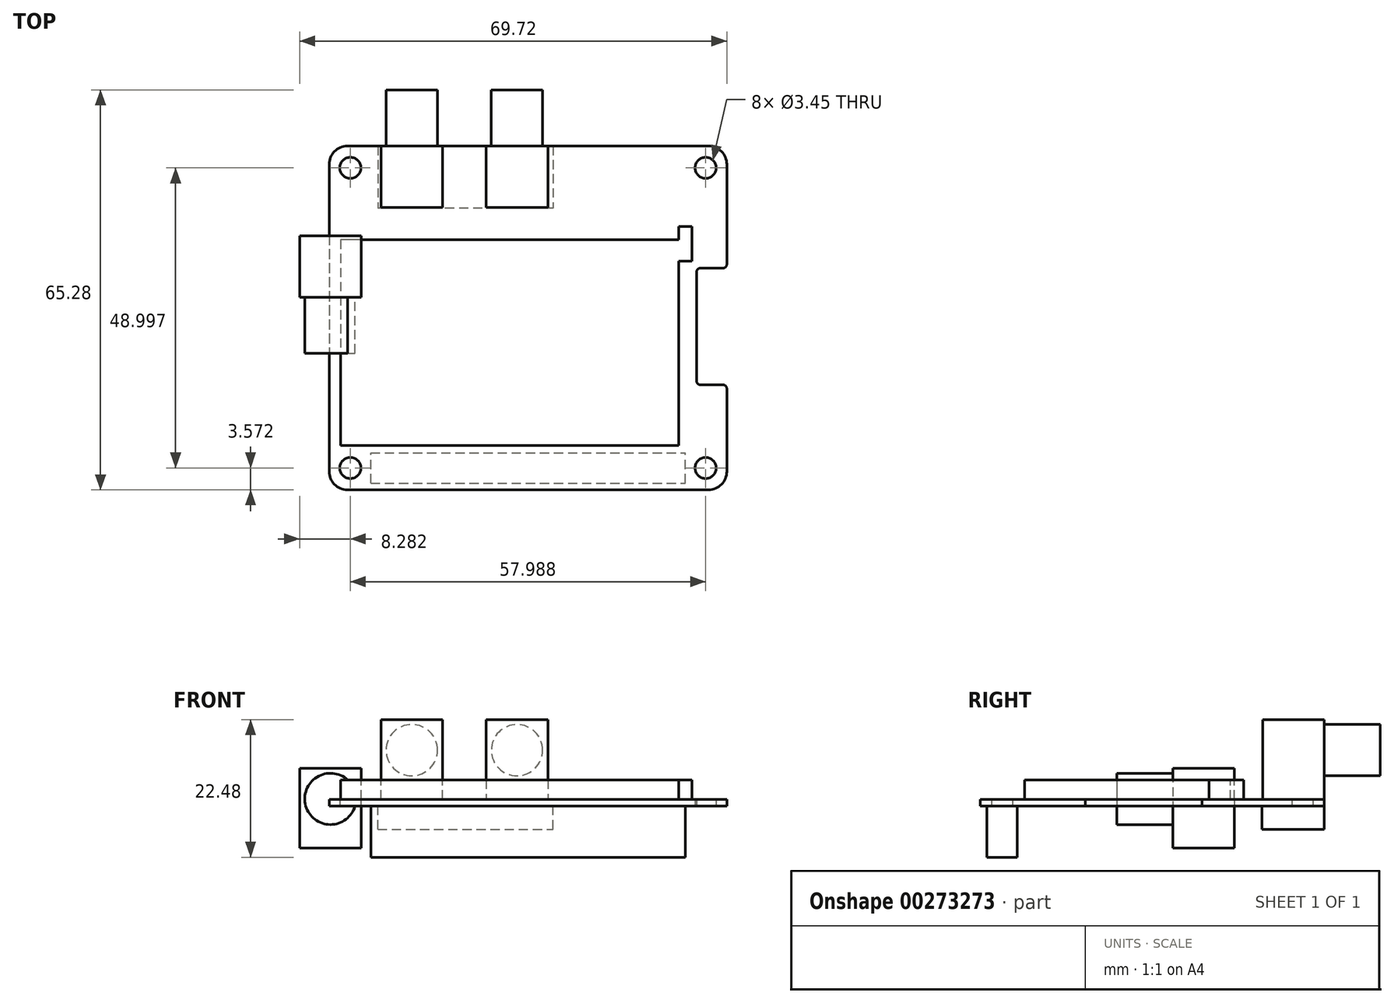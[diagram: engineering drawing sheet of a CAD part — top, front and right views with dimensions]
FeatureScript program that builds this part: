
annotation { "Feature Type Name" : "Feature", "Feature Type Description" : "" }
export const myFeature = defineFeature(function(context is Context, id is Id, definition is map)
    precondition{}
    {
        {
            var Q0;
            Q0=qCreatedBy(makeId("Top.planeOp"),FACE);
            var sketch = newSketch(context, id + "F0", { "sketchPlane" : qUnion([Q0])});
            skLineSegment(sketch, "E0.bottom", {"start": v(29.45, -28.07) * mm, "end": v(-29.45, -28.07) * mm});
            skLineSegment(sketch, "E0.top", {"start": v(29.45, 28.07) * mm, "end": v(-29.45, 28.07) * mm});
            skLineSegment(sketch, "E0.left", {"start": v(32.45, -25.07) * mm, "end": v(32.45, 25.07) * mm});
            skLineSegment(sketch, "E0.right", {"start": v(-32.45, 11.56) * mm, "end": v(-32.45, 25.07) * mm});
            skPoint(sketch, "E0.middle", {"position": v(0, 0) * mm});
            skLineSegment(sketch, "E1.bottom", {"start": v(-31.81, 10.92) * mm, "end": v(-28.16, 10.92) * mm});
            skLineSegment(sketch, "E1.top", {"start": v(-31.81, -8.13) * mm, "end": v(-28.16, -8.13) * mm});
            skLineSegment(sketch, "E1.right", {"start": v(-27.52, 10.29) * mm, "end": v(-27.52, -7.5) * mm});
            skPoint(sketch, "E2.visualSharp", {"position": v(-32.45, 28.07) * mm});
            skArc(sketch, "E2.filletArc", {"start": v(-29.45, 28.07) * mm, "mid": v(-31.57, 27.19) * mm, "end": v(-32.45, 25.07) * mm});
            skArc(sketch, "E3.filletArc", {"start": v(-32.45, 11.56) * mm, "mid": v(-32.26, 11.1) * mm, "end": v(-31.81, 10.92) * mm});
            skLineSegment(sketch, "E4", {"start": v(-32.45, -8.76) * mm, "end": v(-32.45, -25.07) * mm});
            skPoint(sketch, "E5.visualSharp", {"position": v(-27.52, 10.92) * mm});
            skArc(sketch, "E5.filletArc", {"start": v(-27.52, 10.29) * mm, "mid": v(-27.7, 10.74) * mm, "end": v(-28.16, 10.92) * mm});
            skPoint(sketch, "E6.visualSharp", {"position": v(-27.52, -8.13) * mm});
            skArc(sketch, "E6.filletArc", {"start": v(-28.16, -8.13) * mm, "mid": v(-27.7, -7.94) * mm, "end": v(-27.52, -7.5) * mm});
            skArc(sketch, "E7.filletArc", {"start": v(-31.81, -8.13) * mm, "mid": v(-32.26, -8.31) * mm, "end": v(-32.45, -8.76) * mm});
            skPoint(sketch, "E8.visualSharp", {"position": v(-32.45, -28.07) * mm});
            skArc(sketch, "E8.filletArc", {"start": v(-32.45, -25.07) * mm, "mid": v(-31.57, -27.19) * mm, "end": v(-29.45, -28.07) * mm});
            skPoint(sketch, "E9.visualSharp", {"position": v(32.45, -28.07) * mm});
            skArc(sketch, "E9.filletArc", {"start": v(29.45, -28.07) * mm, "mid": v(31.57, -27.19) * mm, "end": v(32.45, -25.07) * mm});
            skPoint(sketch, "E10.visualSharp", {"position": v(32.45, 28.07) * mm});
            skArc(sketch, "E10.filletArc", {"start": v(32.45, 25.07) * mm, "mid": v(31.57, 27.19) * mm, "end": v(29.45, 28.07) * mm});
            skCircle(sketch, "E11", {"center": v(29, 24.5) * mm, "radius": 1.73 * mm});
            skCircle(sketch, "E12", {"center": v(29, -24.5) * mm, "radius": 1.73 * mm});
            skCircle(sketch, "E13", {"center": v(-29, -24.5) * mm, "radius": 1.73 * mm});
            skCircle(sketch, "E14", {"center": v(-29, 24.5) * mm, "radius": 1.73 * mm});
            skSolve(sketch);
        }
        {
            var Q0;
            Q0=makeQuery(id+"F0.imprint","IMPRINT",FACE,{"disambiguationData":[TD([[makeQuery(id+"F0.imprint","IMPRINT",EDGE,{"derivedFrom":sQuery(id+"F0.wireOp",EDGE,"E0.bottom")}),-1.0]])]});
            extrude(context, id + "F1", {"entities" : qUnion([Q0]), "depth" : 1.07 * mm});
        }
        {
            var Q0;
            Q0=makeQuery(id+"F1.opExtrude","SWEPT_FACE",FACE,{"disambiguationData":[OSD([sQuery(id+"F0.wireOp",EDGE,"E0.bottom")])]});
            var sketch = newSketch(context, id + "F2", { "sketchPlane" : qUnion([Q0])});
            skLineSegment(sketch, "E15.bottom", {"start": v(24, 0) * mm, "end": v(13.93, 0) * mm});
            skLineSegment(sketch, "E15.top", {"start": v(24, 14.1) * mm, "end": v(13.93, 14.1) * mm});
            skLineSegment(sketch, "E15.left", {"start": v(24, 0) * mm, "end": v(24, 14.1) * mm});
            skLineSegment(sketch, "E15.right", {"start": v(13.93, 0) * mm, "end": v(13.93, 14.1) * mm});
            skLineSegment(sketch, "E16.bottom", {"start": v(-3.24, 14.1) * mm, "end": v(6.82, 14.1) * mm});
            skLineSegment(sketch, "E16.top", {"start": v(-3.24, 0) * mm, "end": v(6.82, 0) * mm});
            skLineSegment(sketch, "E16.left", {"start": v(-3.24, 14.1) * mm, "end": v(-3.24, 0) * mm});
            skLineSegment(sketch, "E16.right", {"start": v(6.82, 14.1) * mm, "end": v(6.82, 0) * mm});
            skSolve(sketch);
        }
        {
            var Q0;
            {var subQ0=sQuery(id+"F2.wireOp",EDGE,"E16.bottom");Q0=makeQuery(id+"F2.imprint","IMPRINT",FACE,{"disambiguationData":[TD([[makeQuery(id+"F2.imprint","IMPRINT",EDGE,{"derivedFrom":subQ0}),-1.0]])]});}
            var Q1;
            {var subQ0=sQuery(id+"F2.wireOp",EDGE,"E15.top");Q1=makeQuery(id+"F2.imprint","IMPRINT",FACE,{"disambiguationData":[TD([[makeQuery(id+"F2.imprint","IMPRINT",EDGE,{"derivedFrom":subQ0}),1.0]])]});}
            extrude(context, id + "F3", {"entities" : qUnion([Q0, Q1]), "oppositeDirection" : true, "depth" : 10.03 * mm});
        }
        {
            var Q0;
            Q0=makeQuery(id+"F3.opExtrude","CAP_FACE",FACE,{"disambiguationData":[OSD([sQuery(id+"F0.wireOp",EDGE,"E0.bottom"),sQuery(id+"F2.wireOp",EDGE,"E15.top"),sQuery(id+"F2.wireOp",EDGE,"E15.left"),sQuery(id+"F2.wireOp",EDGE,"E15.right")])],"isStart":true});
            var sketch = newSketch(context, id + "F4", { "sketchPlane" : qUnion([Q0])});
            skCircle(sketch, "E17", {"center": v(18.96, 9.1) * mm, "radius": 4.2 * mm});
            skPoint(sketch, "E17.centerSnap0", {"position": v(18.96, 14.1) * mm});
            skSolve(sketch);
        }
        {
            var Q0;
            Q0=makeQuery(id+"F3.opExtrude","CAP_FACE",FACE,{"disambiguationData":[OSD([sQuery(id+"F0.wireOp",EDGE,"E0.bottom"),sQuery(id+"F2.wireOp",EDGE,"E16.bottom"),sQuery(id+"F2.wireOp",EDGE,"E16.left"),sQuery(id+"F2.wireOp",EDGE,"E16.right")])],"isStart":true});
            var sketch = newSketch(context, id + "F5", { "sketchPlane" : qUnion([Q0])});
            skCircle(sketch, "E18", {"center": v(1.8, 9.1) * mm, "radius": 4.2 * mm});
            skPoint(sketch, "E18.centerSnap0", {"position": v(1.8, 14.1) * mm});
            skSolve(sketch);
        }
        {
            var Q0;
            Q0=makeQuery(id+"F5.imprint","IMPRINT",FACE,{"disambiguationData":[TD([[makeQuery(id+"F5.imprint","IMPRINT",EDGE,{"derivedFrom":sQuery(id+"F5.wireOp",EDGE,"E18")}),1.0]])]});
            var Q1;
            Q1=makeQuery(id+"F4.imprint","IMPRINT",FACE,{"disambiguationData":[TD([[makeQuery(id+"F4.imprint","IMPRINT",EDGE,{"derivedFrom":sQuery(id+"F4.wireOp",EDGE,"E17")}),1.0]])]});
            extrude(context, id + "F6", {"entities" : qUnion([Q0, Q1]), "operationType" : NewBodyOperationType.ADD, "depth" : 9.14 * mm});
        }
        {
            var Q0;
            Q0=makeQuery(id+"F1.opExtrude","CAP_FACE",FACE,{"disambiguationData":[OSD([sQuery(id+"F0.wireOp",EDGE,"E0.bottom"),sQuery(id+"F0.wireOp",EDGE,"E0.top"),sQuery(id+"F0.wireOp",EDGE,"E0.left"),sQuery(id+"F0.wireOp",EDGE,"E0.right"),sQuery(id+"F0.wireOp",EDGE,"E1.bottom"),sQuery(id+"F0.wireOp",EDGE,"E1.top"),sQuery(id+"F0.wireOp",EDGE,"E1.right"),sQuery(id+"F0.wireOp",EDGE,"E2.filletArc"),sQuery(id+"F0.wireOp",EDGE,"E3.filletArc"),sQuery(id+"F0.wireOp",EDGE,"E4"),sQuery(id+"F0.wireOp",EDGE,"E5.filletArc"),sQuery(id+"F0.wireOp",EDGE,"E6.filletArc"),sQuery(id+"F0.wireOp",EDGE,"E7.filletArc"),sQuery(id+"F0.wireOp",EDGE,"E8.filletArc"),sQuery(id+"F0.wireOp",EDGE,"E9.filletArc"),sQuery(id+"F0.wireOp",EDGE,"E10.filletArc"),sQuery(id+"F0.wireOp",EDGE,"E11"),sQuery(id+"F0.wireOp",EDGE,"E12"),sQuery(id+"F0.wireOp",EDGE,"E13"),sQuery(id+"F0.wireOp",EDGE,"E14")])],"isStart":true});
            var sketch = newSketch(context, id + "F7", { "sketchPlane" : qUnion([Q0])});
            skLineSegment(sketch, "E19", {"start": v(-29, -24.5) * mm, "end": v(29, -24.5) * mm});
            skLineSegment(sketch, "E20.bottom", {"start": v(25.65, -26.97) * mm, "end": v(-25.65, -26.97) * mm});
            skLineSegment(sketch, "E20.top", {"start": v(25.65, -22.02) * mm, "end": v(-25.65, -22.02) * mm});
            skLineSegment(sketch, "E20.left", {"start": v(25.65, -26.97) * mm, "end": v(25.65, -22.02) * mm});
            skLineSegment(sketch, "E20.right", {"start": v(-25.65, -26.97) * mm, "end": v(-25.65, -22.02) * mm});
            skPoint(sketch, "E20.middle", {"position": v(0, -24.5) * mm});
            skPoint(sketch, "E20.middle.positionSnap0", {"position": v(0, -24.5) * mm});
            skPoint(sketch, "E20.centerSnap0", {"position": v(0, -24.5) * mm});
            skSolve(sketch);
        }
        {
            var Q0;
            {var subQ5=sQuery(id+"F7.wireOp",EDGE,"E20.bottom");Q0=makeQuery(id+"F7.imprint","IMPRINT",FACE,{"disambiguationData":[TD([[makeQuery(id+"F7.imprint","IMPRINT",EDGE,{"derivedFrom":subQ5}),-1.0]])]});}
            var Q1;
            {var subQ5=sQuery(id+"F7.wireOp",EDGE,"E20.top");Q1=makeQuery(id+"F7.imprint","IMPRINT",FACE,{"disambiguationData":[TD([[makeQuery(id+"F7.imprint","IMPRINT",EDGE,{"derivedFrom":subQ5}),1.0]])]});}
            extrude(context, id + "F8", {"entities" : qUnion([Q0, Q1]), "depth" : 8.38 * mm});
        }
        {
            var Q0;
            Q0=makeQuery(id+"F1.opExtrude","CAP_FACE",FACE,{"disambiguationData":[OSD([sQuery(id+"F0.wireOp",EDGE,"E0.bottom"),sQuery(id+"F0.wireOp",EDGE,"E0.top"),sQuery(id+"F0.wireOp",EDGE,"E0.left"),sQuery(id+"F0.wireOp",EDGE,"E0.right"),sQuery(id+"F0.wireOp",EDGE,"E1.bottom"),sQuery(id+"F0.wireOp",EDGE,"E1.top"),sQuery(id+"F0.wireOp",EDGE,"E1.right"),sQuery(id+"F0.wireOp",EDGE,"E2.filletArc"),sQuery(id+"F0.wireOp",EDGE,"E3.filletArc"),sQuery(id+"F0.wireOp",EDGE,"E4"),sQuery(id+"F0.wireOp",EDGE,"E5.filletArc"),sQuery(id+"F0.wireOp",EDGE,"E6.filletArc"),sQuery(id+"F0.wireOp",EDGE,"E7.filletArc"),sQuery(id+"F0.wireOp",EDGE,"E8.filletArc"),sQuery(id+"F0.wireOp",EDGE,"E9.filletArc"),sQuery(id+"F0.wireOp",EDGE,"E10.filletArc"),sQuery(id+"F0.wireOp",EDGE,"E11"),sQuery(id+"F0.wireOp",EDGE,"E12"),sQuery(id+"F0.wireOp",EDGE,"E13"),sQuery(id+"F0.wireOp",EDGE,"E14")])],"isStart":false});
            var sketch = newSketch(context, id + "F9", { "sketchPlane" : qUnion([Q0])});
            skLineSegment(sketch, "E21.bottom", {"start": v(-24.57, -12.76) * mm, "end": v(30.58, -12.76) * mm});
            skLineSegment(sketch, "E21.top", {"start": v(-24.57, 20.8) * mm, "end": v(30.58, 20.8) * mm});
            skLineSegment(sketch, "E21.left", {"start": v(-24.57, -12.76) * mm, "end": v(-24.57, 20.8) * mm});
            skLineSegment(sketch, "E21.right", {"start": v(30.58, -12.76) * mm, "end": v(30.58, 20.8) * mm});
            skLineSegment(sketch, "E22.bottom", {"start": v(-24.57, 20.8) * mm, "end": v(25.58, 20.8) * mm});
            skLineSegment(sketch, "E22.top", {"start": v(-24.57, 26.96) * mm, "end": v(25.58, 26.96) * mm});
            skLineSegment(sketch, "E22.left", {"start": v(-24.57, 20.8) * mm, "end": v(-24.57, 26.96) * mm});
            skLineSegment(sketch, "E22.right", {"start": v(25.58, 20.8) * mm, "end": v(25.58, 26.96) * mm});
            skLineSegment(sketch, "E23.bottom", {"start": v(-24.57, -12.76) * mm, "end": v(-4.48, -12.76) * mm});
            skLineSegment(sketch, "E23.top", {"start": v(-24.57, -27.1) * mm, "end": v(-4.48, -27.1) * mm});
            skLineSegment(sketch, "E23.left", {"start": v(-24.57, -12.76) * mm, "end": v(-24.57, -27.1) * mm});
            skLineSegment(sketch, "E23.right", {"start": v(-4.48, -12.76) * mm, "end": v(-4.48, -27.1) * mm});
            skLineSegment(sketch, "E24.bottom", {"start": v(30.58, -12.76) * mm, "end": v(25.86, -12.76) * mm});
            skLineSegment(sketch, "E24.top", {"start": v(30.58, -19.58) * mm, "end": v(25.86, -19.58) * mm});
            skLineSegment(sketch, "E24.left", {"start": v(30.58, -12.76) * mm, "end": v(30.58, -19.58) * mm});
            skLineSegment(sketch, "E24.right", {"start": v(25.86, -12.76) * mm, "end": v(25.86, -19.58) * mm});
            skLineSegment(sketch, "E25.bottom", {"start": v(-24.57, -14.92) * mm, "end": v(-26.79, -14.92) * mm});
            skLineSegment(sketch, "E25.top", {"start": v(-24.57, -9.3) * mm, "end": v(-26.79, -9.3) * mm});
            skLineSegment(sketch, "E25.left", {"start": v(-24.57, -14.92) * mm, "end": v(-24.57, -9.3) * mm});
            skLineSegment(sketch, "E25.right", {"start": v(-26.79, -14.92) * mm, "end": v(-26.79, -9.3) * mm});
            skSolve(sketch);
        }
        {
            var Q0;
            Q0=makeQuery(id+"F9.imprint","IMPRINT",FACE,{"disambiguationData":[TD([[makeQuery(id+"F9.imprint","IMPRINT",EDGE,{"derivedFrom":sQuery(id+"F9.wireOp",EDGE,"E24.bottom")}),1.0]])]});
            var Q1;
            Q1=makeQuery(id+"F9.imprint","IMPRINT",FACE,{"disambiguationData":[TD([[makeQuery(id+"F9.imprint","IMPRINT",EDGE,{"derivedFrom":sQuery(id+"F9.wireOp",EDGE,"E21.bottom")}),1.0]])]});
            var Q2;
            Q2=makeQuery(id+"F9.imprint","IMPRINT",FACE,{"disambiguationData":[TD([[makeQuery(id+"F9.imprint","IMPRINT",EDGE,{"derivedFrom":sQuery(id+"F9.wireOp",EDGE,"E22.bottom")}),1.0]])]});
            var Q3;
            {var subQ1=sQuery(id+"F9.wireOp",EDGE,"E23.bottom");Q3=makeQuery(id+"F9.imprint","IMPRINT",FACE,{"disambiguationData":[TD([[makeQuery(id+"F9.imprint","IMPRINT",EDGE,{"derivedFrom":subQ1}),-1.0]])]});}
            var Q4;
            {var subQ2=sQuery(id+"F9.wireOp",EDGE,"E25.bottom");Q4=makeQuery(id+"F9.imprint","IMPRINT",FACE,{"disambiguationData":[TD([[makeQuery(id+"F9.imprint","IMPRINT",EDGE,{"derivedFrom":subQ2}),-1.0]])]});}
            extrude(context, id + "F10", {"entities" : qUnion([Q0, Q1, Q2, Q3, Q4]), "depth" : 3.17 * mm});
        }
        {
            var Q0;
            Q0=makeQuery(id+"F1.opExtrude","CAP_FACE",FACE,{"disambiguationData":[OSD([sQuery(id+"F0.wireOp",EDGE,"E0.bottom"),sQuery(id+"F0.wireOp",EDGE,"E0.top"),sQuery(id+"F0.wireOp",EDGE,"E0.left"),sQuery(id+"F0.wireOp",EDGE,"E0.right"),sQuery(id+"F0.wireOp",EDGE,"E1.bottom"),sQuery(id+"F0.wireOp",EDGE,"E1.top"),sQuery(id+"F0.wireOp",EDGE,"E1.right"),sQuery(id+"F0.wireOp",EDGE,"E2.filletArc"),sQuery(id+"F0.wireOp",EDGE,"E3.filletArc"),sQuery(id+"F0.wireOp",EDGE,"E4"),sQuery(id+"F0.wireOp",EDGE,"E5.filletArc"),sQuery(id+"F0.wireOp",EDGE,"E6.filletArc"),sQuery(id+"F0.wireOp",EDGE,"E7.filletArc"),sQuery(id+"F0.wireOp",EDGE,"E8.filletArc"),sQuery(id+"F0.wireOp",EDGE,"E9.filletArc"),sQuery(id+"F0.wireOp",EDGE,"E10.filletArc"),sQuery(id+"F0.wireOp",EDGE,"E11"),sQuery(id+"F0.wireOp",EDGE,"E12"),sQuery(id+"F0.wireOp",EDGE,"E13"),sQuery(id+"F0.wireOp",EDGE,"E14")])],"isStart":true});
            var sketch = newSketch(context, id + "F11", { "sketchPlane" : qUnion([Q0])});
            skLineSegment(sketch, "E26.bottom", {"start": v(-4.06, 28.07) * mm, "end": v(24.51, 28.07) * mm});
            skLineSegment(sketch, "E26.top", {"start": v(-4.06, 17.9) * mm, "end": v(24.51, 17.9) * mm});
            skLineSegment(sketch, "E26.left", {"start": v(-4.06, 28.07) * mm, "end": v(-4.06, 17.9) * mm});
            skLineSegment(sketch, "E26.right", {"start": v(24.51, 28.07) * mm, "end": v(24.51, 17.9) * mm});
            skSolve(sketch);
        }
        {
            var Q0;
            Q0=makeQuery(id+"F11.imprint","IMPRINT",FACE,{"disambiguationData":[TD([[makeQuery(id+"F11.imprint","IMPRINT",EDGE,{"derivedFrom":sQuery(id+"F11.wireOp",EDGE,"E26.bottom")}),1.0]])]});
            extrude(context, id + "F12", {"entities" : qUnion([Q0]), "depth" : 3.8 * mm});
        }
        {
            var Q0;
            Q0=makeQuery(id+"F1.opExtrude","CAP_FACE",FACE,{"disambiguationData":[OSD([sQuery(id+"F0.wireOp",EDGE,"E0.bottom"),sQuery(id+"F0.wireOp",EDGE,"E0.top"),sQuery(id+"F0.wireOp",EDGE,"E0.left"),sQuery(id+"F0.wireOp",EDGE,"E0.right"),sQuery(id+"F0.wireOp",EDGE,"E1.bottom"),sQuery(id+"F0.wireOp",EDGE,"E1.top"),sQuery(id+"F0.wireOp",EDGE,"E1.right"),sQuery(id+"F0.wireOp",EDGE,"E2.filletArc"),sQuery(id+"F0.wireOp",EDGE,"E3.filletArc"),sQuery(id+"F0.wireOp",EDGE,"E4"),sQuery(id+"F0.wireOp",EDGE,"E5.filletArc"),sQuery(id+"F0.wireOp",EDGE,"E6.filletArc"),sQuery(id+"F0.wireOp",EDGE,"E7.filletArc"),sQuery(id+"F0.wireOp",EDGE,"E8.filletArc"),sQuery(id+"F0.wireOp",EDGE,"E9.filletArc"),sQuery(id+"F0.wireOp",EDGE,"E10.filletArc"),sQuery(id+"F0.wireOp",EDGE,"E11"),sQuery(id+"F0.wireOp",EDGE,"E12"),sQuery(id+"F0.wireOp",EDGE,"E13"),sQuery(id+"F0.wireOp",EDGE,"E14")])],"isStart":false});
            var sketch = newSketch(context, id + "F13", { "sketchPlane" : qUnion([Q0])});
            skPoint(sketch, "E27", {"position": v(-29, 24.5) * mm});
            skSolve(sketch);
        }
        {
            var Q0;
            Q0=makeQuery(id+"F1.opExtrude","SWEPT_BODY",BODY,{"disambiguationData":[OSD([sQuery(id+"F0.wireOp",EDGE,"E0.bottom"),sQuery(id+"F0.wireOp",EDGE,"E0.top"),sQuery(id+"F0.wireOp",EDGE,"E0.left"),sQuery(id+"F0.wireOp",EDGE,"E0.right"),sQuery(id+"F0.wireOp",EDGE,"E1.bottom"),sQuery(id+"F0.wireOp",EDGE,"E1.top"),sQuery(id+"F0.wireOp",EDGE,"E1.right"),sQuery(id+"F0.wireOp",EDGE,"E2.filletArc"),sQuery(id+"F0.wireOp",EDGE,"E3.filletArc"),sQuery(id+"F0.wireOp",EDGE,"E4"),sQuery(id+"F0.wireOp",EDGE,"E5.filletArc"),sQuery(id+"F0.wireOp",EDGE,"E6.filletArc"),sQuery(id+"F0.wireOp",EDGE,"E7.filletArc"),sQuery(id+"F0.wireOp",EDGE,"E8.filletArc"),sQuery(id+"F0.wireOp",EDGE,"E9.filletArc"),sQuery(id+"F0.wireOp",EDGE,"E10.filletArc"),sQuery(id+"F0.wireOp",EDGE,"E11"),sQuery(id+"F0.wireOp",EDGE,"E12"),sQuery(id+"F0.wireOp",EDGE,"E13"),sQuery(id+"F0.wireOp",EDGE,"E14")])]});
            var Q1;
            Q1=makeQuery(id+"F3.opExtrude","SWEPT_BODY",BODY,{"disambiguationData":[OSD([sQuery(id+"F0.wireOp",EDGE,"E0.bottom"),sQuery(id+"F2.wireOp",EDGE,"E15.top"),sQuery(id+"F2.wireOp",EDGE,"E15.left"),sQuery(id+"F2.wireOp",EDGE,"E15.right")])]});
            var Q2;
            Q2=makeQuery(id+"F3.opExtrude","SWEPT_BODY",BODY,{"disambiguationData":[OSD([sQuery(id+"F0.wireOp",EDGE,"E0.bottom"),sQuery(id+"F2.wireOp",EDGE,"E16.bottom"),sQuery(id+"F2.wireOp",EDGE,"E16.left"),sQuery(id+"F2.wireOp",EDGE,"E16.right")])]});
            var Q3;
            Q3=makeQuery(id+"F10.opExtrude","SWEPT_BODY",BODY,{"disambiguationData":[OSD([sQuery(id+"F9.wireOp",EDGE,"E21.bottom"),sQuery(id+"F9.wireOp",EDGE,"E21.top"),sQuery(id+"F9.wireOp",EDGE,"E21.left"),sQuery(id+"F9.wireOp",EDGE,"E21.right"),sQuery(id+"F9.wireOp",EDGE,"E22.top"),sQuery(id+"F9.wireOp",EDGE,"E22.left"),sQuery(id+"F9.wireOp",EDGE,"E22.right"),sQuery(id+"F9.wireOp",EDGE,"E23.top"),sQuery(id+"F9.wireOp",EDGE,"E23.left"),sQuery(id+"F9.wireOp",EDGE,"E23.right"),sQuery(id+"F9.wireOp",EDGE,"E24.top"),sQuery(id+"F9.wireOp",EDGE,"E24.left"),sQuery(id+"F9.wireOp",EDGE,"E24.right"),sQuery(id+"F9.wireOp",EDGE,"E25.bottom"),sQuery(id+"F9.wireOp",EDGE,"E25.top"),sQuery(id+"F9.wireOp",EDGE,"E25.right")])]});
            var Q4;
            Q4=makeQuery(id+"F12.opExtrude","SWEPT_BODY",BODY,{"disambiguationData":[OSD([sQuery(id+"F11.wireOp",EDGE,"E26.bottom"),sQuery(id+"F11.wireOp",EDGE,"E26.top"),sQuery(id+"F11.wireOp",EDGE,"E26.left"),sQuery(id+"F11.wireOp",EDGE,"E26.right")])]});
            var Q5;
            Q5=makeQuery(id+"F8.opExtrude","SWEPT_BODY",BODY,{"disambiguationData":[OSD([sQuery(id+"F7.wireOp",EDGE,"E20.bottom"),sQuery(id+"F7.wireOp",EDGE,"E20.top"),sQuery(id+"F7.wireOp",EDGE,"E20.left"),sQuery(id+"F7.wireOp",EDGE,"E20.right")])]});
            var Q6;
            Q6=sQuery(id+"F13.wireOp",VERTEX,"E27");
            var Q7;
            Q7=qCreatedBy(makeId("Origin.pointOp"),VERTEX);
            transform(context, id + "F14", {"entities" : qUnion([Q0, Q1, Q2, Q3, Q4, Q5]), "transformType" : TransformType.TRANSLATION_ENTITY, "oppositeDirectionEntity" : false, "transformLine" : qUnion([Q6, Q7]), "makeCopy" : false});
        }
        {
            var Q0;
            Q0=makeQuery(id+"F1.opExtrude","SWEPT_BODY",BODY,{"disambiguationData":[OSD([sQuery(id+"F0.wireOp",EDGE,"E0.bottom"),sQuery(id+"F0.wireOp",EDGE,"E0.top"),sQuery(id+"F0.wireOp",EDGE,"E0.left"),sQuery(id+"F0.wireOp",EDGE,"E0.right"),sQuery(id+"F0.wireOp",EDGE,"E1.bottom"),sQuery(id+"F0.wireOp",EDGE,"E1.top"),sQuery(id+"F0.wireOp",EDGE,"E1.right"),sQuery(id+"F0.wireOp",EDGE,"E2.filletArc"),sQuery(id+"F0.wireOp",EDGE,"E3.filletArc"),sQuery(id+"F0.wireOp",EDGE,"E4"),sQuery(id+"F0.wireOp",EDGE,"E5.filletArc"),sQuery(id+"F0.wireOp",EDGE,"E6.filletArc"),sQuery(id+"F0.wireOp",EDGE,"E7.filletArc"),sQuery(id+"F0.wireOp",EDGE,"E8.filletArc"),sQuery(id+"F0.wireOp",EDGE,"E9.filletArc"),sQuery(id+"F0.wireOp",EDGE,"E10.filletArc"),sQuery(id+"F0.wireOp",EDGE,"E11"),sQuery(id+"F0.wireOp",EDGE,"E12"),sQuery(id+"F0.wireOp",EDGE,"E13"),sQuery(id+"F0.wireOp",EDGE,"E14")])]});
            var Q1;
            Q1=makeQuery(id+"F3.opExtrude","SWEPT_BODY",BODY,{"disambiguationData":[OSD([sQuery(id+"F0.wireOp",EDGE,"E0.bottom"),sQuery(id+"F2.wireOp",EDGE,"E15.top"),sQuery(id+"F2.wireOp",EDGE,"E15.left"),sQuery(id+"F2.wireOp",EDGE,"E15.right")])]});
            var Q2;
            Q2=makeQuery(id+"F3.opExtrude","SWEPT_BODY",BODY,{"disambiguationData":[OSD([sQuery(id+"F0.wireOp",EDGE,"E0.bottom"),sQuery(id+"F2.wireOp",EDGE,"E16.bottom"),sQuery(id+"F2.wireOp",EDGE,"E16.left"),sQuery(id+"F2.wireOp",EDGE,"E16.right")])]});
            var Q3;
            Q3=makeQuery(id+"F10.opExtrude","SWEPT_BODY",BODY,{"disambiguationData":[OSD([sQuery(id+"F9.wireOp",EDGE,"E21.bottom"),sQuery(id+"F9.wireOp",EDGE,"E21.top"),sQuery(id+"F9.wireOp",EDGE,"E21.left"),sQuery(id+"F9.wireOp",EDGE,"E21.right"),sQuery(id+"F9.wireOp",EDGE,"E22.top"),sQuery(id+"F9.wireOp",EDGE,"E22.left"),sQuery(id+"F9.wireOp",EDGE,"E22.right"),sQuery(id+"F9.wireOp",EDGE,"E23.top"),sQuery(id+"F9.wireOp",EDGE,"E23.left"),sQuery(id+"F9.wireOp",EDGE,"E23.right"),sQuery(id+"F9.wireOp",EDGE,"E24.top"),sQuery(id+"F9.wireOp",EDGE,"E24.left"),sQuery(id+"F9.wireOp",EDGE,"E24.right"),sQuery(id+"F9.wireOp",EDGE,"E25.bottom"),sQuery(id+"F9.wireOp",EDGE,"E25.top"),sQuery(id+"F9.wireOp",EDGE,"E25.right")])]});
            var Q4;
            Q4=makeQuery(id+"F12.opExtrude","SWEPT_BODY",BODY,{"disambiguationData":[OSD([sQuery(id+"F11.wireOp",EDGE,"E26.bottom"),sQuery(id+"F11.wireOp",EDGE,"E26.top"),sQuery(id+"F11.wireOp",EDGE,"E26.left"),sQuery(id+"F11.wireOp",EDGE,"E26.right")])]});
            var Q5;
            Q5=makeQuery(id+"F8.opExtrude","SWEPT_BODY",BODY,{"disambiguationData":[OSD([sQuery(id+"F7.wireOp",EDGE,"E20.bottom"),sQuery(id+"F7.wireOp",EDGE,"E20.top"),sQuery(id+"F7.wireOp",EDGE,"E20.left"),sQuery(id+"F7.wireOp",EDGE,"E20.right")])]});
            transform(context, id + "F15", {"entities" : qUnion([Q0, Q1, Q2, Q3, Q4, Q5]), "transformType" : TransformType.TRANSLATION_3D, "dx" : 22.21 * mm, "dy" : -6.93 * mm, "dz" : 0 * mm, "makeCopy" : false});
        }
        {
            var Q0;
            Q0=makeQuery(id+"F1.opExtrude","SWEPT_BODY",BODY,{"disambiguationData":[OSD([sQuery(id+"F0.wireOp",EDGE,"E0.bottom"),sQuery(id+"F0.wireOp",EDGE,"E0.top"),sQuery(id+"F0.wireOp",EDGE,"E0.left"),sQuery(id+"F0.wireOp",EDGE,"E0.right"),sQuery(id+"F0.wireOp",EDGE,"E1.bottom"),sQuery(id+"F0.wireOp",EDGE,"E1.top"),sQuery(id+"F0.wireOp",EDGE,"E1.right"),sQuery(id+"F0.wireOp",EDGE,"E2.filletArc"),sQuery(id+"F0.wireOp",EDGE,"E3.filletArc"),sQuery(id+"F0.wireOp",EDGE,"E4"),sQuery(id+"F0.wireOp",EDGE,"E5.filletArc"),sQuery(id+"F0.wireOp",EDGE,"E6.filletArc"),sQuery(id+"F0.wireOp",EDGE,"E7.filletArc"),sQuery(id+"F0.wireOp",EDGE,"E8.filletArc"),sQuery(id+"F0.wireOp",EDGE,"E9.filletArc"),sQuery(id+"F0.wireOp",EDGE,"E10.filletArc"),sQuery(id+"F0.wireOp",EDGE,"E11"),sQuery(id+"F0.wireOp",EDGE,"E12"),sQuery(id+"F0.wireOp",EDGE,"E13"),sQuery(id+"F0.wireOp",EDGE,"E14")])]});
            var Q1;
            Q1=makeQuery(id+"F3.opExtrude","SWEPT_BODY",BODY,{"disambiguationData":[OSD([sQuery(id+"F0.wireOp",EDGE,"E0.bottom"),sQuery(id+"F2.wireOp",EDGE,"E15.top"),sQuery(id+"F2.wireOp",EDGE,"E15.left"),sQuery(id+"F2.wireOp",EDGE,"E15.right")])]});
            var Q2;
            Q2=makeQuery(id+"F3.opExtrude","SWEPT_BODY",BODY,{"disambiguationData":[OSD([sQuery(id+"F0.wireOp",EDGE,"E0.bottom"),sQuery(id+"F2.wireOp",EDGE,"E16.bottom"),sQuery(id+"F2.wireOp",EDGE,"E16.left"),sQuery(id+"F2.wireOp",EDGE,"E16.right")])]});
            var Q3;
            Q3=makeQuery(id+"F8.opExtrude","SWEPT_BODY",BODY,{"disambiguationData":[OSD([sQuery(id+"F7.wireOp",EDGE,"E20.bottom"),sQuery(id+"F7.wireOp",EDGE,"E20.top"),sQuery(id+"F7.wireOp",EDGE,"E20.left"),sQuery(id+"F7.wireOp",EDGE,"E20.right")])]});
            var Q4;
            Q4=makeQuery(id+"F10.opExtrude","SWEPT_BODY",BODY,{"disambiguationData":[OSD([sQuery(id+"F9.wireOp",EDGE,"E21.bottom"),sQuery(id+"F9.wireOp",EDGE,"E21.top"),sQuery(id+"F9.wireOp",EDGE,"E21.left"),sQuery(id+"F9.wireOp",EDGE,"E21.right"),sQuery(id+"F9.wireOp",EDGE,"E22.top"),sQuery(id+"F9.wireOp",EDGE,"E22.left"),sQuery(id+"F9.wireOp",EDGE,"E22.right"),sQuery(id+"F9.wireOp",EDGE,"E23.top"),sQuery(id+"F9.wireOp",EDGE,"E23.left"),sQuery(id+"F9.wireOp",EDGE,"E23.right"),sQuery(id+"F9.wireOp",EDGE,"E24.top"),sQuery(id+"F9.wireOp",EDGE,"E24.left"),sQuery(id+"F9.wireOp",EDGE,"E24.right"),sQuery(id+"F9.wireOp",EDGE,"E25.bottom"),sQuery(id+"F9.wireOp",EDGE,"E25.top"),sQuery(id+"F9.wireOp",EDGE,"E25.right")])]});
            var Q5;
            Q5=makeQuery(id+"F12.opExtrude","SWEPT_BODY",BODY,{"disambiguationData":[OSD([sQuery(id+"F11.wireOp",EDGE,"E26.bottom"),sQuery(id+"F11.wireOp",EDGE,"E26.top"),sQuery(id+"F11.wireOp",EDGE,"E26.left"),sQuery(id+"F11.wireOp",EDGE,"E26.right")])]});
            transform(context, id + "F16", {"entities" : qUnion([Q0, Q1, Q2, Q3, Q4, Q5]), "transformType" : TransformType.TRANSLATION_3D, "dx" : 0 * mm, "dy" : 0 * mm, "dz" : 9.02 * mm, "makeCopy" : false});
        }
        {
            var Q0;
            Q0=makeQuery(id+"F1.opExtrude","CAP_FACE",FACE,{"disambiguationData":[OSD([sQuery(id+"F0.wireOp",EDGE,"E0.bottom"),sQuery(id+"F0.wireOp",EDGE,"E0.top"),sQuery(id+"F0.wireOp",EDGE,"E0.left"),sQuery(id+"F0.wireOp",EDGE,"E0.right"),sQuery(id+"F0.wireOp",EDGE,"E1.bottom"),sQuery(id+"F0.wireOp",EDGE,"E1.top"),sQuery(id+"F0.wireOp",EDGE,"E1.right"),sQuery(id+"F0.wireOp",EDGE,"E2.filletArc"),sQuery(id+"F0.wireOp",EDGE,"E3.filletArc"),sQuery(id+"F0.wireOp",EDGE,"E4"),sQuery(id+"F0.wireOp",EDGE,"E5.filletArc"),sQuery(id+"F0.wireOp",EDGE,"E6.filletArc"),sQuery(id+"F0.wireOp",EDGE,"E7.filletArc"),sQuery(id+"F0.wireOp",EDGE,"E8.filletArc"),sQuery(id+"F0.wireOp",EDGE,"E9.filletArc"),sQuery(id+"F0.wireOp",EDGE,"E10.filletArc"),sQuery(id+"F0.wireOp",EDGE,"E11"),sQuery(id+"F0.wireOp",EDGE,"E12"),sQuery(id+"F0.wireOp",EDGE,"E13"),sQuery(id+"F0.wireOp",EDGE,"E14")])],"isStart":false});
            var sketch = newSketch(context, id + "F17", { "sketchPlane" : qUnion([Q0])});
            skPoint(sketch, "E28", {"position": v(22.21, -6.93) * mm});
            skPoint(sketch, "E29", {"position": v(80.2, -55.93) * mm});
            skSolve(sketch);
        }
        {
            var Q0;
            Q0=makeQuery(id+"F1.opExtrude","SWEPT_BODY",BODY,{"disambiguationData":[OSD([sQuery(id+"F0.wireOp",EDGE,"E0.bottom"),sQuery(id+"F0.wireOp",EDGE,"E0.top"),sQuery(id+"F0.wireOp",EDGE,"E0.left"),sQuery(id+"F0.wireOp",EDGE,"E0.right"),sQuery(id+"F0.wireOp",EDGE,"E1.bottom"),sQuery(id+"F0.wireOp",EDGE,"E1.top"),sQuery(id+"F0.wireOp",EDGE,"E1.right"),sQuery(id+"F0.wireOp",EDGE,"E2.filletArc"),sQuery(id+"F0.wireOp",EDGE,"E3.filletArc"),sQuery(id+"F0.wireOp",EDGE,"E4"),sQuery(id+"F0.wireOp",EDGE,"E5.filletArc"),sQuery(id+"F0.wireOp",EDGE,"E6.filletArc"),sQuery(id+"F0.wireOp",EDGE,"E7.filletArc"),sQuery(id+"F0.wireOp",EDGE,"E8.filletArc"),sQuery(id+"F0.wireOp",EDGE,"E9.filletArc"),sQuery(id+"F0.wireOp",EDGE,"E10.filletArc"),sQuery(id+"F0.wireOp",EDGE,"E11"),sQuery(id+"F0.wireOp",EDGE,"E12"),sQuery(id+"F0.wireOp",EDGE,"E13"),sQuery(id+"F0.wireOp",EDGE,"E14")])]});
            var Q1;
            Q1=makeQuery(id+"F3.opExtrude","SWEPT_BODY",BODY,{"disambiguationData":[OSD([sQuery(id+"F0.wireOp",EDGE,"E0.bottom"),sQuery(id+"F2.wireOp",EDGE,"E15.top"),sQuery(id+"F2.wireOp",EDGE,"E15.left"),sQuery(id+"F2.wireOp",EDGE,"E15.right")])]});
            var Q2;
            Q2=makeQuery(id+"F3.opExtrude","SWEPT_BODY",BODY,{"disambiguationData":[OSD([sQuery(id+"F0.wireOp",EDGE,"E0.bottom"),sQuery(id+"F2.wireOp",EDGE,"E16.bottom"),sQuery(id+"F2.wireOp",EDGE,"E16.left"),sQuery(id+"F2.wireOp",EDGE,"E16.right")])]});
            var Q3;
            Q3=makeQuery(id+"F8.opExtrude","SWEPT_BODY",BODY,{"disambiguationData":[OSD([sQuery(id+"F7.wireOp",EDGE,"E20.bottom"),sQuery(id+"F7.wireOp",EDGE,"E20.top"),sQuery(id+"F7.wireOp",EDGE,"E20.left"),sQuery(id+"F7.wireOp",EDGE,"E20.right")])]});
            var Q4;
            Q4=makeQuery(id+"F10.opExtrude","SWEPT_BODY",BODY,{"disambiguationData":[OSD([sQuery(id+"F9.wireOp",EDGE,"E21.bottom"),sQuery(id+"F9.wireOp",EDGE,"E21.top"),sQuery(id+"F9.wireOp",EDGE,"E21.left"),sQuery(id+"F9.wireOp",EDGE,"E21.right"),sQuery(id+"F9.wireOp",EDGE,"E22.top"),sQuery(id+"F9.wireOp",EDGE,"E22.left"),sQuery(id+"F9.wireOp",EDGE,"E22.right"),sQuery(id+"F9.wireOp",EDGE,"E23.top"),sQuery(id+"F9.wireOp",EDGE,"E23.left"),sQuery(id+"F9.wireOp",EDGE,"E23.right"),sQuery(id+"F9.wireOp",EDGE,"E24.top"),sQuery(id+"F9.wireOp",EDGE,"E24.left"),sQuery(id+"F9.wireOp",EDGE,"E24.right"),sQuery(id+"F9.wireOp",EDGE,"E25.bottom"),sQuery(id+"F9.wireOp",EDGE,"E25.top"),sQuery(id+"F9.wireOp",EDGE,"E25.right")])]});
            var Q5;
            Q5=makeQuery(id+"F12.opExtrude","SWEPT_BODY",BODY,{"disambiguationData":[OSD([sQuery(id+"F11.wireOp",EDGE,"E26.bottom"),sQuery(id+"F11.wireOp",EDGE,"E26.top"),sQuery(id+"F11.wireOp",EDGE,"E26.left"),sQuery(id+"F11.wireOp",EDGE,"E26.right")])]});
            var Q6;
            Q6=sQuery(id+"F17.wireOp",VERTEX,"E29");
            var Q7;
            Q7=sQuery(id+"F17.wireOp",VERTEX,"E28");
            transform(context, id + "F18", {"entities" : qUnion([Q0, Q1, Q2, Q3, Q4, Q5]), "transformType" : TransformType.TRANSLATION_ENTITY, "oppositeDirectionEntity" : false, "transformLine" : qUnion([Q6, Q7]), "makeCopy" : false});
        }
        {
            var Q0;
            Q0=makeQuery(id+"F1.opExtrude","SWEPT_BODY",BODY,{"disambiguationData":[OSD([sQuery(id+"F0.wireOp",EDGE,"E0.bottom"),sQuery(id+"F0.wireOp",EDGE,"E0.top"),sQuery(id+"F0.wireOp",EDGE,"E0.left"),sQuery(id+"F0.wireOp",EDGE,"E0.right"),sQuery(id+"F0.wireOp",EDGE,"E1.bottom"),sQuery(id+"F0.wireOp",EDGE,"E1.top"),sQuery(id+"F0.wireOp",EDGE,"E1.right"),sQuery(id+"F0.wireOp",EDGE,"E2.filletArc"),sQuery(id+"F0.wireOp",EDGE,"E3.filletArc"),sQuery(id+"F0.wireOp",EDGE,"E4"),sQuery(id+"F0.wireOp",EDGE,"E5.filletArc"),sQuery(id+"F0.wireOp",EDGE,"E6.filletArc"),sQuery(id+"F0.wireOp",EDGE,"E7.filletArc"),sQuery(id+"F0.wireOp",EDGE,"E8.filletArc"),sQuery(id+"F0.wireOp",EDGE,"E9.filletArc"),sQuery(id+"F0.wireOp",EDGE,"E10.filletArc"),sQuery(id+"F0.wireOp",EDGE,"E11"),sQuery(id+"F0.wireOp",EDGE,"E12"),sQuery(id+"F0.wireOp",EDGE,"E13"),sQuery(id+"F0.wireOp",EDGE,"E14")])]});
            var Q1;
            Q1=makeQuery(id+"F3.opExtrude","SWEPT_BODY",BODY,{"disambiguationData":[OSD([sQuery(id+"F0.wireOp",EDGE,"E0.bottom"),sQuery(id+"F2.wireOp",EDGE,"E15.top"),sQuery(id+"F2.wireOp",EDGE,"E15.left"),sQuery(id+"F2.wireOp",EDGE,"E15.right")])]});
            var Q2;
            Q2=makeQuery(id+"F3.opExtrude","SWEPT_BODY",BODY,{"disambiguationData":[OSD([sQuery(id+"F0.wireOp",EDGE,"E0.bottom"),sQuery(id+"F2.wireOp",EDGE,"E16.bottom"),sQuery(id+"F2.wireOp",EDGE,"E16.left"),sQuery(id+"F2.wireOp",EDGE,"E16.right")])]});
            var Q3;
            Q3=makeQuery(id+"F8.opExtrude","SWEPT_BODY",BODY,{"disambiguationData":[OSD([sQuery(id+"F7.wireOp",EDGE,"E20.bottom"),sQuery(id+"F7.wireOp",EDGE,"E20.top"),sQuery(id+"F7.wireOp",EDGE,"E20.left"),sQuery(id+"F7.wireOp",EDGE,"E20.right")])]});
            var Q4;
            Q4=makeQuery(id+"F10.opExtrude","SWEPT_BODY",BODY,{"disambiguationData":[OSD([sQuery(id+"F9.wireOp",EDGE,"E21.bottom"),sQuery(id+"F9.wireOp",EDGE,"E21.top"),sQuery(id+"F9.wireOp",EDGE,"E21.left"),sQuery(id+"F9.wireOp",EDGE,"E21.right"),sQuery(id+"F9.wireOp",EDGE,"E22.top"),sQuery(id+"F9.wireOp",EDGE,"E22.left"),sQuery(id+"F9.wireOp",EDGE,"E22.right"),sQuery(id+"F9.wireOp",EDGE,"E23.top"),sQuery(id+"F9.wireOp",EDGE,"E23.left"),sQuery(id+"F9.wireOp",EDGE,"E23.right"),sQuery(id+"F9.wireOp",EDGE,"E24.top"),sQuery(id+"F9.wireOp",EDGE,"E24.left"),sQuery(id+"F9.wireOp",EDGE,"E24.right"),sQuery(id+"F9.wireOp",EDGE,"E25.bottom"),sQuery(id+"F9.wireOp",EDGE,"E25.top"),sQuery(id+"F9.wireOp",EDGE,"E25.right")])]});
            var Q5;
            Q5=makeQuery(id+"F12.opExtrude","SWEPT_BODY",BODY,{"disambiguationData":[OSD([sQuery(id+"F11.wireOp",EDGE,"E26.bottom"),sQuery(id+"F11.wireOp",EDGE,"E26.top"),sQuery(id+"F11.wireOp",EDGE,"E26.left"),sQuery(id+"F11.wireOp",EDGE,"E26.right")])]});
            var Q6;
            Q6=makeQuery(id+"F1.opExtrude","CAP_EDGE",EDGE,{"disambiguationData":[OSD([sQuery(id+"F0.wireOp",EDGE,"E12")])],"isStart":false});
            transform(context, id + "F19", {"entities" : qUnion([Q0, Q1, Q2, Q3, Q4, Q5]), "transformType" : TransformType.ROTATION, "transformAxis" : qUnion([Q6]), "angle" : 180 * degree, "makeCopy" : false});
        }
    });
